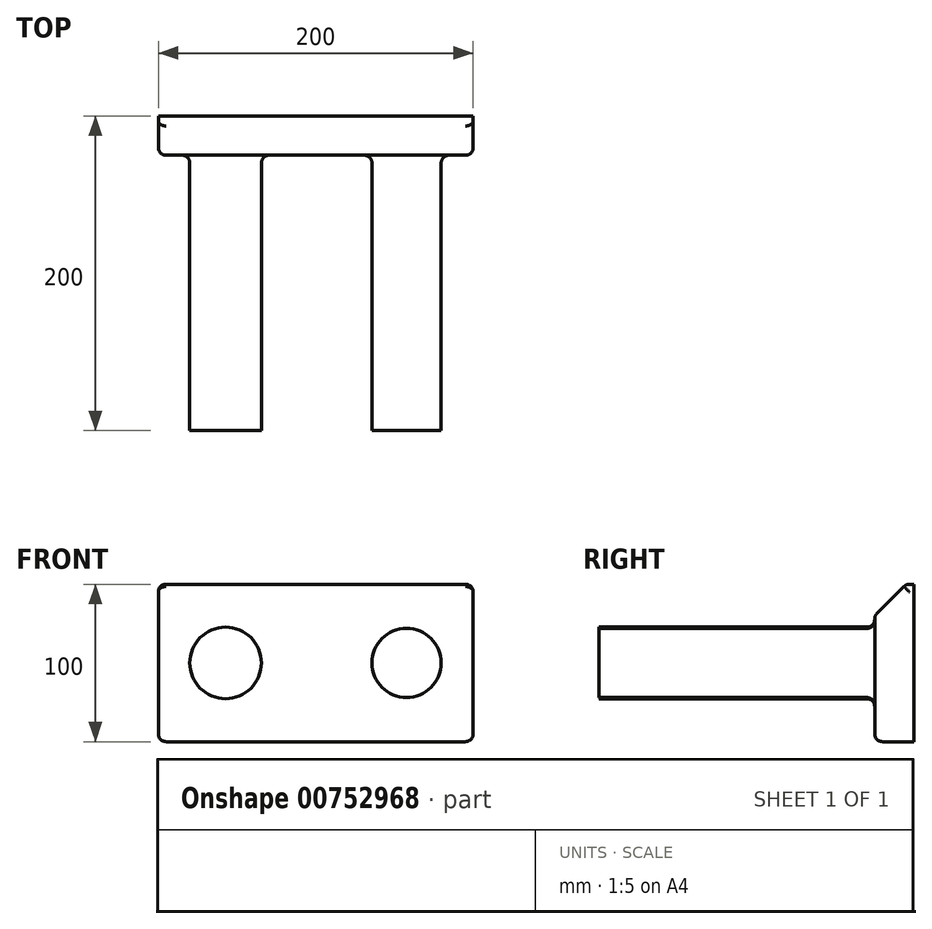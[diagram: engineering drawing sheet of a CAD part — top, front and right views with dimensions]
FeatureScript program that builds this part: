
annotation { "Feature Type Name" : "Feature", "Feature Type Description" : "" }
export const myFeature = defineFeature(function(context is Context, id is Id, definition is map)
    precondition{}
    {
        {
            var Q0;
            Q0=qCreatedBy(makeId("Front.planeOp"),FACE);
            var sketch = newSketch(context, id + "F0", { "sketchPlane" : qUnion([Q0])});
            skLineSegment(sketch, "E0.bottom", {"start": v(86.97, -79.69) * mm, "end": v(-113.03, -79.69) * mm});
            skLineSegment(sketch, "E0.top", {"start": v(86.97, 20.31) * mm, "end": v(-113.03, 20.31) * mm});
            skLineSegment(sketch, "E0.left", {"start": v(86.97, -79.69) * mm, "end": v(86.97, 20.31) * mm});
            skLineSegment(sketch, "E0.right", {"start": v(-113.03, -79.69) * mm, "end": v(-113.03, 20.31) * mm});
            skCircle(sketch, "E1", {"center": v(44.63, -29.69) * mm, "radius": 21.96 * mm});
            skPoint(sketch, "E1.centerSnap0", {"position": v(86.97, -29.69) * mm});
            skCircle(sketch, "E2", {"center": v(-70.3, -29.69) * mm, "radius": 22.72 * mm});
            skPoint(sketch, "E2.centerSnap0", {"position": v(-113.03, -29.69) * mm});
            skSolve(sketch);
        }
        {
            var Q0;
            Q0 = qSketchRegion(id + "F0", true);
            extrude(context, id + "F1", {"entities" : qUnion([Q0]), "depth" : 25 * mm, "offsetDistance" : 25 * mm});
        }
        {
            var Q0;
            Q0=makeQuery(id+"F0.imprint","IMPRINT",FACE,{"disambiguationData":[TD([[makeQuery(id+"F0.imprint","IMPRINT",EDGE,{"derivedFrom":sQuery(id+"F0.wireOp",EDGE,"E1")}),1.0]])]});
            var Q1;
            Q1=makeQuery(id+"F0.imprint","IMPRINT",FACE,{"disambiguationData":[TD([[makeQuery(id+"F0.imprint","IMPRINT",EDGE,{"derivedFrom":sQuery(id+"F0.wireOp",EDGE,"E2")}),1.0]])]});
            extrude(context, id + "F2", {"entities" : qUnion([Q0, Q1]), "operationType" : NewBodyOperationType.ADD, "depth" : 200 * mm, "offsetDistance" : 25 * mm});
        }
        {
            var Q0;
            Q0=makeQuery(id+"F1.opExtrude","CAP_EDGE",EDGE,{"disambiguationData":[OSD([sQuery(id+"F0.wireOp",EDGE,"E0.top")])],"isStart":false});
            chamfer(context, id + "F3", {"entities" : qUnion([Q0]), "width" : 20 * mm, "tangentPropagation" : true});
        }
        {
            var Q0;
            {var subQ0=sQuery(id+"F0.wireOp",EDGE,"E0.top");Q0=makeQuery(id+"F3.opChamfer","BLEND_EDGE",EDGE,{"blendedFrom":[makeQuery(id+"F1.opExtrude","CAP_EDGE",EDGE,{"disambiguationData":[OSD([subQ0])],"isStart":false}),makeQuery(id+"F1.opExtrude","CAP_FACE",FACE,{"disambiguationData":[OSD([sQuery(id+"F0.wireOp",EDGE,"E0.bottom"),subQ0,sQuery(id+"F0.wireOp",EDGE,"E0.left"),sQuery(id+"F0.wireOp",EDGE,"E0.right"),sQuery(id+"F0.wireOp",EDGE,"E1"),sQuery(id+"F0.wireOp",EDGE,"E2")])],"isStart":false})],"blendedInto":[makeQuery(id+"F1.opExtrude","CAP_FACE",FACE,{"disambiguationData":[OSD([sQuery(id+"F0.wireOp",EDGE,"E0.bottom"),subQ0,sQuery(id+"F0.wireOp",EDGE,"E0.left"),sQuery(id+"F0.wireOp",EDGE,"E0.right"),sQuery(id+"F0.wireOp",EDGE,"E1"),sQuery(id+"F0.wireOp",EDGE,"E2")])],"isStart":false})]});}
            var Q1;
            {var subQ0=sQuery(id+"F0.wireOp",EDGE,"E0.top");Q1=makeQuery(id+"F3.opChamfer","BLEND_EDGE",EDGE,{"blendedFrom":[makeQuery(id+"F1.opExtrude","CAP_EDGE",EDGE,{"disambiguationData":[OSD([subQ0])],"isStart":false}),makeQuery(id+"F1.opExtrude","SWEPT_FACE",FACE,{"disambiguationData":[OSD([subQ0])]})],"blendedInto":[makeQuery(id+"F1.opExtrude","SWEPT_FACE",FACE,{"disambiguationData":[OSD([subQ0])]})]});}
            var Q2;
            Q2=makeQuery(id+"F1.opExtrude","CAP_FACE",FACE,{"disambiguationData":[OSD([sQuery(id+"F0.wireOp",EDGE,"E0.bottom"),sQuery(id+"F0.wireOp",EDGE,"E0.top"),sQuery(id+"F0.wireOp",EDGE,"E0.left"),sQuery(id+"F0.wireOp",EDGE,"E0.right"),sQuery(id+"F0.wireOp",EDGE,"E1"),sQuery(id+"F0.wireOp",EDGE,"E2")])],"isStart":false});
            var Q3;
            Q3=makeQuery(id+"F3.opChamfer","BLEND_EDGE",EDGE,{"blendedFrom":[makeQuery(id+"F1.opExtrude","CAP_EDGE",EDGE,{"disambiguationData":[OSD([sQuery(id+"F0.wireOp",EDGE,"E0.top")])],"isStart":false}),makeQuery(id+"F1.opExtrude","SWEPT_FACE",FACE,{"disambiguationData":[OSD([sQuery(id+"F0.wireOp",EDGE,"E0.right")])]})],"blendedInto":[makeQuery(id+"F1.opExtrude","SWEPT_FACE",FACE,{"disambiguationData":[OSD([sQuery(id+"F0.wireOp",EDGE,"E0.right")])]})]});
            var Q4;
            Q4=makeQuery(id+"F3.opChamfer","BLEND_EDGE",EDGE,{"blendedFrom":[makeQuery(id+"F1.opExtrude","CAP_EDGE",EDGE,{"disambiguationData":[OSD([sQuery(id+"F0.wireOp",EDGE,"E0.top")])],"isStart":false}),makeQuery(id+"F1.opExtrude","SWEPT_FACE",FACE,{"disambiguationData":[OSD([sQuery(id+"F0.wireOp",EDGE,"E0.left")])]})],"blendedInto":[makeQuery(id+"F1.opExtrude","SWEPT_FACE",FACE,{"disambiguationData":[OSD([sQuery(id+"F0.wireOp",EDGE,"E0.left")])]})]});
            var Q5;
            Q5=makeQuery(id+"F1.opExtrude","SWEPT_EDGE",EDGE,{"disambiguationData":[OSD([sQuery(id+"F0.wireOp",EDGE,"E0.bottom"),sQuery(id+"F0.wireOp",EDGE,"E0.left")])]});
            var Q6;
            Q6=makeQuery(id+"F1.opExtrude","SWEPT_EDGE",EDGE,{"disambiguationData":[OSD([sQuery(id+"F0.wireOp",EDGE,"E0.bottom"),sQuery(id+"F0.wireOp",EDGE,"E0.right")])]});
            fillet(context, id + "F4", {"entities" : qUnion([Q0, Q1, Q2, Q3, Q4, Q5, Q6]), "radius" : 5 * mm, "tangentPropagation" : true, "allowEdgeOverflow" : false});
        }
        {
            var Q0;
            {var subQ0=sQuery(id+"F0.wireOp",EDGE,"E0.top");Q0=makeQuery(id+"F4.opFillet","BLEND_EDGE",EDGE,{"blendedFrom":[makeQuery(id+"F3.opChamfer","BLEND_EDGE",EDGE,{"blendedFrom":[makeQuery(id+"F1.opExtrude","CAP_EDGE",EDGE,{"disambiguationData":[OSD([subQ0])],"isStart":false}),makeQuery(id+"F1.opExtrude","SWEPT_FACE",FACE,{"disambiguationData":[OSD([sQuery(id+"F0.wireOp",EDGE,"E0.right")])]})],"blendedInto":[makeQuery(id+"F1.opExtrude","SWEPT_FACE",FACE,{"disambiguationData":[OSD([sQuery(id+"F0.wireOp",EDGE,"E0.right")])]})]}),makeQuery(id+"F1.opExtrude","SWEPT_FACE",FACE,{"disambiguationData":[OSD([subQ0])]})],"blendedInto":[makeQuery(id+"F1.opExtrude","SWEPT_FACE",FACE,{"disambiguationData":[OSD([subQ0])]})]});}
            var Q1;
            {var subQ0=sQuery(id+"F0.wireOp",EDGE,"E0.top");var subQ1=makeQuery(id+"F1.opExtrude","SWEPT_FACE",FACE,{"disambiguationData":[OSD([subQ0])]});Q1=makeQuery(id+"F4.opFillet","BLEND_EDGE",EDGE,{"blendedFrom":[makeQuery(id+"F3.opChamfer","BLEND_EDGE",EDGE,{"blendedFrom":[makeQuery(id+"F1.opExtrude","CAP_EDGE",EDGE,{"disambiguationData":[OSD([subQ0])],"isStart":false}),subQ1],"blendedInto":[subQ1]}),subQ1],"blendedInto":[subQ1]});}
            var Q2;
            {var subQ0=sQuery(id+"F0.wireOp",EDGE,"E0.top");var subQ1=makeQuery(id+"F1.opExtrude","CAP_EDGE",EDGE,{"disambiguationData":[OSD([subQ0])],"isStart":false});Q2=makeQuery(id+"F4.opFillet","BLEND_EDGE",EDGE,{"blendedFrom":[makeQuery(id+"F3.opChamfer","BLEND_EDGE",EDGE,{"blendedFrom":[subQ1,makeQuery(id+"F1.opExtrude","SWEPT_FACE",FACE,{"disambiguationData":[OSD([subQ0])]})],"blendedInto":[makeQuery(id+"F1.opExtrude","SWEPT_FACE",FACE,{"disambiguationData":[OSD([subQ0])]})]}),makeQuery(id+"F3.opChamfer","BLEND_EDGE",EDGE,{"blendedFrom":[subQ1,makeQuery(id+"F1.opExtrude","SWEPT_FACE",FACE,{"disambiguationData":[OSD([sQuery(id+"F0.wireOp",EDGE,"E0.left")])]})],"blendedInto":[makeQuery(id+"F1.opExtrude","SWEPT_FACE",FACE,{"disambiguationData":[OSD([sQuery(id+"F0.wireOp",EDGE,"E0.left")])]})]})],"blendedInto":[]});}
            fillet(context, id + "F5", {"entities" : qUnion([Q0, Q1, Q2]), "radius" : 5 * mm, "tangentPropagation" : true, "allowEdgeOverflow" : false});
        }
    });
